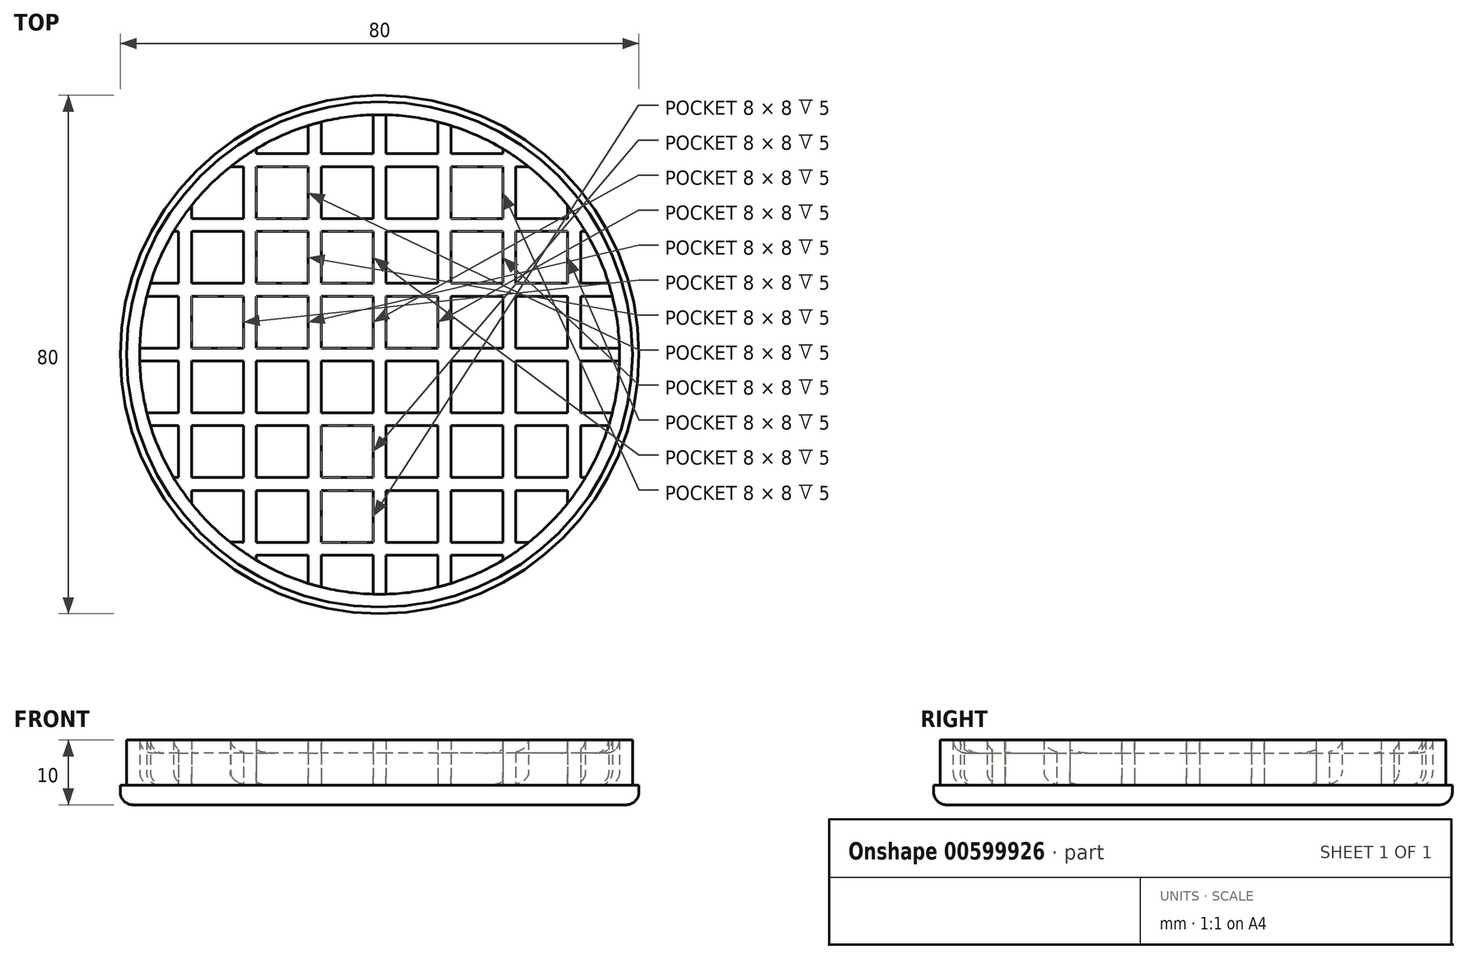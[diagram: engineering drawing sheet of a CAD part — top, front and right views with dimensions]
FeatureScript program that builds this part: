
annotation { "Feature Type Name" : "Feature", "Feature Type Description" : "" }
export const myFeature = defineFeature(function(context is Context, id is Id, definition is map)
    precondition{}
    {
        {
            var Q0;
            Q0=qCreatedBy(makeId("Front.planeOp"),FACE);
            var sketch = newSketch(context, id + "F0", { "sketchPlane" : qUnion([Q0])});
            skLineSegment(sketch, "E0", {"start": v(0, 0) * mm, "end": v(-38, 0) * mm});
            skLineSegment(sketch, "E1", {"start": v(-40, 2) * mm, "end": v(-40, 3) * mm});
            skLineSegment(sketch, "E2", {"start": v(-40, 3) * mm, "end": v(-39, 3) * mm});
            skLineSegment(sketch, "E3", {"start": v(-39, 3) * mm, "end": v(-39, 10) * mm});
            skLineSegment(sketch, "E4", {"start": v(-39, 10) * mm, "end": v(-37, 10) * mm});
            skLineSegment(sketch, "E5", {"start": v(0, 3) * mm, "end": v(0, 0) * mm});
            skPoint(sketch, "E6.visualSharp", {"position": v(-37, 3) * mm});
            skPoint(sketch, "E7.visualSharp", {"position": v(-40, 0) * mm});
            skArc(sketch, "E7.filletArc", {"start": v(-40, 2) * mm, "mid": v(-39.41, 0.59) * mm, "end": v(-38, 0) * mm});
            skLineSegment(sketch, "E8", {"start": v(-37, 10) * mm, "end": v(-37, 3) * mm});
            skLineSegment(sketch, "E9", {"start": v(-37, 3) * mm, "end": v(0, 3) * mm});
            skSolve(sketch);
        }
        {
            var Q0;
            Q0=makeQuery(id+"F0.imprint","IMPRINT",FACE,{"disambiguationData":[TD([[makeQuery(id+"F0.imprint","IMPRINT",EDGE,{"derivedFrom":sQuery(id+"F0.wireOp",EDGE,"E0")}),-1.0]])]});
            var Q1;
            Q1=sQuery(id+"F0.wireOp",EDGE,"E5");
            revolve(context, id + "F1", {"entities" : qUnion([Q0]), "axis" : qUnion([Q1]), "revolveType" : RevolveType.FULL});
        }
        {
            var Q0;
            Q0=makeQuery(id+"F1.opRevolve","SWEPT_FACE",FACE,{"disambiguationData":[OSD([sQuery(id+"F0.wireOp",EDGE,"E9")])]});
            var sketch = newSketch(context, id + "F2", { "sketchPlane" : qUnion([Q0])});
            skLineSegment(sketch, "E10", {"start": v(-1, 37.14) * mm, "end": v(-1, 21) * mm});
            skLineSegment(sketch, "E11", {"start": v(-9, 36.05) * mm, "end": v(-9, 31) * mm});
            skLineSegment(sketch, "E12", {"start": v(-19, 31.93) * mm, "end": v(-19, 31) * mm});
            skLineSegment(sketch, "E13", {"start": v(-11, 35.49) * mm, "end": v(-11, 31) * mm});
            skLineSegment(sketch, "E14", {"start": v(0, 63.51) * mm, "end": v(0, 19) * mm, "construction": true});
            skLineSegment(sketch, "E15.MirrorCS", {"start": v(29, 23.22) * mm, "end": v(29, 21) * mm});
            skLineSegment(sketch, "E16.MirrorCS", {"start": v(19, 31.93) * mm, "end": v(19, 31) * mm});
            skLineSegment(sketch, "E17.MirrorCS", {"start": v(11, 35.49) * mm, "end": v(11, 31) * mm});
            skLineSegment(sketch, "E18.MirrorCS", {"start": v(9, 36.05) * mm, "end": v(9, 31) * mm});
            skLineSegment(sketch, "E19.MirrorCS", {"start": v(1, 37.14) * mm, "end": v(1, 31) * mm});
            skArc(sketch, "E20", {"start": v(-9, 36.05) * mm, "mid": v(-10, 35.78) * mm, "end": v(-11, 35.49) * mm});
            skLineSegment(sketch, "E21", {"start": v(-46.87, 0) * mm, "end": v(0, 0) * mm, "construction": true});
            skLineSegment(sketch, "E22", {"start": v(-37.14, -1) * mm, "end": v(-31, -1) * mm});
            skLineSegment(sketch, "E23", {"start": v(-36.05, -9) * mm, "end": v(-31, -9) * mm});
            skLineSegment(sketch, "E24", {"start": v(-35.49, -11) * mm, "end": v(-31, -11) * mm});
            skLineSegment(sketch, "E25", {"start": v(-31.93, -19) * mm, "end": v(-31, -19) * mm});
            skLineSegment(sketch, "E26", {"start": v(-19, -31) * mm, "end": v(-11, -31) * mm});
            skLineSegment(sketch, "E27.MirrorCS", {"start": v(-37.14, 1) * mm, "end": v(-31, 1) * mm});
            skLineSegment(sketch, "E28.MirrorCS", {"start": v(-36.05, 9) * mm, "end": v(-31, 9) * mm});
            skLineSegment(sketch, "E29.MirrorCS", {"start": v(-31.93, 19) * mm, "end": v(-31, 19) * mm});
            skPoint(sketch, "E30.orphan", {"position": v(-11, 50.12) * mm});
            skPoint(sketch, "E31.orphan", {"position": v(-9, 38.7) * mm});
            skPoint(sketch, "E32.orphan", {"position": v(-1, 41.9) * mm});
            skPoint(sketch, "E33.orphan", {"position": v(1, 41.9) * mm});
            skPoint(sketch, "E34.orphan", {"position": v(9, 38.7) * mm});
            skPoint(sketch, "E35.orphan", {"position": v(11, 50.12) * mm});
            skPoint(sketch, "E36.orphan", {"position": v(-19, 39.94) * mm});
            skArc(sketch, "E37.trimOffspring", {"start": v(-19, 31.93) * mm, "mid": v(-21.16, 30.54) * mm, "end": v(-23.22, 29) * mm});
            skArc(sketch, "E38.trimOffspring", {"start": v(1, 37.14) * mm, "mid": v(0, 37.15) * mm, "end": v(-1, 37.14) * mm});
            skArc(sketch, "E39.trimOffspring", {"start": v(11, 35.49) * mm, "mid": v(10, 35.78) * mm, "end": v(9, 36.05) * mm});
            skPoint(sketch, "E40.orphan", {"position": v(21, 41.25) * mm});
            skPoint(sketch, "E41.orphan", {"position": v(19, 39.94) * mm});
            skPoint(sketch, "E42.orphan", {"position": v(22.5, 31) * mm});
            skPoint(sketch, "E43.orphan", {"position": v(28.03, 29) * mm});
            skLineSegment(sketch, "E44.trimOffspring", {"start": v(9, 29) * mm, "end": v(9, 21) * mm});
            skLineSegment(sketch, "E45.trimOffspring", {"start": v(11, 29) * mm, "end": v(19, 29) * mm});
            skLineSegment(sketch, "E46.trimOffspring", {"start": v(19, 29) * mm, "end": v(19, 21) * mm});
            skLineSegment(sketch, "E47.trimOffspring", {"start": v(21, 29) * mm, "end": v(23.22, 29) * mm});
            skLineSegment(sketch, "E48.trimOffspring", {"start": v(29, 19) * mm, "end": v(29, 11) * mm});
            skLineSegment(sketch, "E49.trimOffspring", {"start": v(31, 19) * mm, "end": v(31, 11) * mm});
            skLineSegment(sketch, "E50.trimOffspring", {"start": v(31, 19) * mm, "end": v(31.93, 19) * mm});
            skPoint(sketch, "E51.orphan", {"position": v(31, 33.97) * mm});
            skPoint(sketch, "E52.orphan", {"position": v(36.83, 21) * mm});
            skPoint(sketch, "E53.orphan", {"position": v(35.98, 19) * mm});
            skPoint(sketch, "E54.orphan", {"position": v(29, 34.3) * mm});
            skPoint(sketch, "E55.orphan", {"position": v(43.35, 11) * mm});
            skPoint(sketch, "E56.orphan", {"position": v(42.56, 9) * mm});
            skArc(sketch, "E57.trimOffspring", {"start": v(31.93, 19) * mm, "mid": v(30.54, 21.16) * mm, "end": v(29, 23.22) * mm});
            skArc(sketch, "E58.trimOffspring", {"start": v(23.22, 29) * mm, "mid": v(21.16, 30.54) * mm, "end": v(19, 31.93) * mm});
            skLineSegment(sketch, "E59", {"start": v(11, 31) * mm, "end": v(19, 31) * mm});
            skLineSegment(sketch, "E60.trimOffspring", {"start": v(21, 21) * mm, "end": v(29, 21) * mm});
            skLineSegment(sketch, "E61.trimOffspring", {"start": v(19, 19) * mm, "end": v(19, 11) * mm});
            skLineSegment(sketch, "E62.trimOffspring", {"start": v(21, 19) * mm, "end": v(21, 11) * mm});
            skLineSegment(sketch, "E63.trimOffspring", {"start": v(0, 11) * mm, "end": v(0, -20.11) * mm, "construction": true});
            skLineSegment(sketch, "E64.trimOffspring", {"start": v(11, 19) * mm, "end": v(11, 11) * mm});
            skLineSegment(sketch, "E65.trimOffspring", {"start": v(21, 19) * mm, "end": v(29, 19) * mm});
            skLineSegment(sketch, "E66.trimOffspring", {"start": v(9, 9) * mm, "end": v(9, 1) * mm});
            skLineSegment(sketch, "E67.trimOffspring", {"start": v(11, 19) * mm, "end": v(19, 19) * mm});
            skLineSegment(sketch, "E68", {"start": v(11, 29) * mm, "end": v(11, 21) * mm});
            skLineSegment(sketch, "E69.trimOffspring", {"start": v(11, 21) * mm, "end": v(19, 21) * mm});
            skLineSegment(sketch, "E70.trimOffspring", {"start": v(1, 21) * mm, "end": v(9, 21) * mm});
            skLineSegment(sketch, "E71.trimOffspring", {"start": v(1, 19) * mm, "end": v(1, 11) * mm});
            skLineSegment(sketch, "E72.trimOffspring", {"start": v(-1, 19) * mm, "end": v(-1, 11) * mm});
            skLineSegment(sketch, "E73.trimOffspring", {"start": v(1, 19) * mm, "end": v(9, 19) * mm});
            skLineSegment(sketch, "E74.trimOffspring", {"start": v(-9, 21) * mm, "end": v(-1, 21) * mm});
            skLineSegment(sketch, "E75.trimOffspring", {"start": v(-11, 19) * mm, "end": v(-11, 11) * mm});
            skLineSegment(sketch, "E76.trimOffspring", {"start": v(-9, 19) * mm, "end": v(-1, 19) * mm});
            skLineSegment(sketch, "E77.trimOffspring", {"start": v(-9, 19) * mm, "end": v(-9, 11) * mm});
            skLineSegment(sketch, "E78.trimOffspring", {"start": v(-9, 31) * mm, "end": v(-1, 31) * mm});
            skLineSegment(sketch, "E79.trimOffspring", {"start": v(-9, 29) * mm, "end": v(-9, 21) * mm});
            skLineSegment(sketch, "E80.trimOffspring", {"start": v(-9, 29) * mm, "end": v(-1, 29) * mm});
            skLineSegment(sketch, "E81.trimOffspring", {"start": v(-11, 29) * mm, "end": v(-11, 21) * mm});
            skLineSegment(sketch, "E82.trimOffspring", {"start": v(-9, 11) * mm, "end": v(-1, 11) * mm});
            skLineSegment(sketch, "E83.trimOffspring", {"start": v(-11, 9) * mm, "end": v(-11, 1) * mm});
            skLineSegment(sketch, "E84.trimOffspring", {"start": v(-9, 9) * mm, "end": v(-9, 1) * mm});
            skLineSegment(sketch, "E85", {"start": v(-19, 9) * mm, "end": v(-11, 9) * mm});
            skLineSegment(sketch, "E86.trimOffspring", {"start": v(-19, 11) * mm, "end": v(-11, 11) * mm});
            skLineSegment(sketch, "E87.trimOffspring", {"start": v(-21, 9) * mm, "end": v(-21, 1) * mm});
            skLineSegment(sketch, "E88.trimOffspring", {"start": v(-19, 9) * mm, "end": v(-19, 1) * mm});
            skLineSegment(sketch, "E89.trimOffspring", {"start": v(-31, 9) * mm, "end": v(-31, 1) * mm});
            skLineSegment(sketch, "E90.trimOffspring", {"start": v(-29, 11) * mm, "end": v(-21, 11) * mm});
            skLineSegment(sketch, "E91.trimOffspring", {"start": v(-29, 9) * mm, "end": v(-29, 1) * mm});
            skLineSegment(sketch, "E92.trimOffspring", {"start": v(-29, 9) * mm, "end": v(-21, 9) * mm});
            skLineSegment(sketch, "E93.trimOffspring", {"start": v(-31, 19) * mm, "end": v(-31, 11) * mm});
            skLineSegment(sketch, "E94.trimOffspring", {"start": v(-29, 21) * mm, "end": v(-21, 21) * mm});
            skPoint(sketch, "E95.MirrorCS.start.orphan", {"position": v(-37.13, 21) * mm});
            skLineSegment(sketch, "E96.trimOffspring", {"start": v(-29, 19) * mm, "end": v(-21, 19) * mm});
            skLineSegment(sketch, "E97.trimOffspring", {"start": v(-29, 19) * mm, "end": v(-29, 11) * mm});
            skPoint(sketch, "E98.orphan", {"position": v(-37.52, 19) * mm});
            skArc(sketch, "E99.trimOffspring", {"start": v(-35.49, 11) * mm, "mid": v(-35.78, 10) * mm, "end": v(-36.05, 9) * mm});
            skArc(sketch, "E100.trimOffspring", {"start": v(-29, 23.22) * mm, "mid": v(-30.54, 21.16) * mm, "end": v(-31.93, 19) * mm});
            skLineSegment(sketch, "E101.trimOffspring", {"start": v(-19, 31) * mm, "end": v(-11, 31) * mm});
            skPoint(sketch, "E102.MirrorCS.start.orphan", {"position": v(-27.7, 31) * mm});
            skPoint(sketch, "E103.start.orphan", {"position": v(-21, 41.25) * mm});
            skLineSegment(sketch, "E104.trimOffspring", {"start": v(-23.22, 29) * mm, "end": v(-21, 29) * mm});
            skLineSegment(sketch, "E105.trimOffspring", {"start": v(-19, 29) * mm, "end": v(-11, 29) * mm});
            skLineSegment(sketch, "E106.trimOffspring", {"start": v(-19, 29) * mm, "end": v(-19, 21) * mm});
            skArc(sketch, "E107.trimOffspring", {"start": v(36.05, 9) * mm, "mid": v(35.78, 10) * mm, "end": v(35.49, 11) * mm});
            skArc(sketch, "E108.trimOffspring", {"start": v(37.14, -1) * mm, "mid": v(37.15, 0) * mm, "end": v(37.14, 1) * mm});
            skLineSegment(sketch, "E109.trimOffspring", {"start": v(31, 1) * mm, "end": v(37.14, 1) * mm});
            skLineSegment(sketch, "E110.trimOffspring", {"start": v(29, -1) * mm, "end": v(29, -9) * mm});
            skLineSegment(sketch, "E111.trimOffspring", {"start": v(31, -1) * mm, "end": v(31, -9) * mm});
            skLineSegment(sketch, "E112.trimOffspring", {"start": v(37.15, 0) * mm, "end": v(44.83, 0) * mm, "construction": true});
            skLineSegment(sketch, "E113.trimOffspring", {"start": v(31, 9) * mm, "end": v(31, 1) * mm});
            skLineSegment(sketch, "E114.trimOffspring", {"start": v(31, 11) * mm, "end": v(35.49, 11) * mm});
            skLineSegment(sketch, "E115.trimOffspring", {"start": v(31, 9) * mm, "end": v(36.05, 9) * mm});
            skLineSegment(sketch, "E116.trimOffspring", {"start": v(29, 9) * mm, "end": v(29, 1) * mm});
            skLineSegment(sketch, "E117.trimOffspring", {"start": v(21, 9) * mm, "end": v(21, 1) * mm});
            skLineSegment(sketch, "E118.trimOffspring", {"start": v(21, 11) * mm, "end": v(29, 11) * mm});
            skLineSegment(sketch, "E119.trimOffspring", {"start": v(19, 9) * mm, "end": v(19, 1) * mm});
            skLineSegment(sketch, "E120.trimOffspring", {"start": v(21, 9) * mm, "end": v(29, 9) * mm});
            skLineSegment(sketch, "E121", {"start": v(9, 11) * mm, "end": v(9, 19) * mm});
            skLineSegment(sketch, "E122.trimOffspring", {"start": v(11, 9) * mm, "end": v(11, 1) * mm});
            skLineSegment(sketch, "E123.trimOffspring", {"start": v(11, 11) * mm, "end": v(19, 11) * mm});
            skLineSegment(sketch, "E124.trimOffspring", {"start": v(11, 9) * mm, "end": v(19, 9) * mm});
            skLineSegment(sketch, "E125.trimOffspring", {"start": v(1, 11) * mm, "end": v(9, 11) * mm});
            skLineSegment(sketch, "E126.trimOffspring", {"start": v(1, 9) * mm, "end": v(9, 9) * mm});
            skLineSegment(sketch, "E127.trimOffspring", {"start": v(1, 9) * mm, "end": v(1, 1) * mm});
            skLineSegment(sketch, "E128.trimOffspring", {"start": v(-1, 9) * mm, "end": v(-1, 1) * mm});
            skLineSegment(sketch, "E129", {"start": v(-19, 21) * mm, "end": v(-11, 21) * mm});
            skLineSegment(sketch, "E130.trimOffspring", {"start": v(-21, 19) * mm, "end": v(-21, 11) * mm});
            skLineSegment(sketch, "E131.trimOffspring", {"start": v(-19, 19) * mm, "end": v(-11, 19) * mm});
            skLineSegment(sketch, "E132.trimOffspring", {"start": v(-19, 19) * mm, "end": v(-19, 11) * mm});
            skLineSegment(sketch, "E133", {"start": v(-21, 29) * mm, "end": v(-21, 21) * mm});
            skLineSegment(sketch, "E134.trimOffspring", {"start": v(-31, -1) * mm, "end": v(-31, -9) * mm});
            skPoint(sketch, "E135.orphan", {"position": v(-42.4, 11) * mm});
            skLineSegment(sketch, "E136.trimOffspring", {"start": v(-29, 1) * mm, "end": v(-21, 1) * mm});
            skLineSegment(sketch, "E137.trimOffspring", {"start": v(-29, -1) * mm, "end": v(-29, -9) * mm});
            skPoint(sketch, "E138.orphan", {"position": v(-41.5, 1) * mm});
            skPoint(sketch, "E139.orphan", {"position": v(-41.5, -1) * mm});
            skArc(sketch, "E140.trimOffspring", {"start": v(-37.14, 1) * mm, "mid": v(-37.15, 0) * mm, "end": v(-37.14, -1) * mm});
            skArc(sketch, "E141.trimOffspring", {"start": v(-36.05, -9) * mm, "mid": v(-35.78, -10) * mm, "end": v(-35.49, -11) * mm});
            skPoint(sketch, "E142.orphan", {"position": v(-38.6, 9) * mm});
            skLineSegment(sketch, "E143.trimOffspring", {"start": v(-29, 23.22) * mm, "end": v(-29, 21) * mm});
            skPoint(sketch, "E144.MirrorCS.start.orphan", {"position": v(-33.6, 29) * mm});
            skPoint(sketch, "E145.start.orphan", {"position": v(-31, 33.97) * mm});
            skPoint(sketch, "E146.start.orphan", {"position": v(-29, 34.3) * mm});
            skPoint(sketch, "E147.orphan", {"position": v(-38.6, -9) * mm});
            skPoint(sketch, "E148.orphan", {"position": v(-42.4, -11) * mm});
            skArc(sketch, "E149.trimOffspring", {"start": v(-31.93, -19) * mm, "mid": v(-30.54, -21.16) * mm, "end": v(-29, -23.22) * mm});
            skLineSegment(sketch, "E150.trimOffspring", {"start": v(-29, -9) * mm, "end": v(-21, -9) * mm});
            skLineSegment(sketch, "E151.trimOffspring", {"start": v(-31, -11) * mm, "end": v(-31, -19) * mm});
            skLineSegment(sketch, "E152.trimOffspring", {"start": v(-29, -11) * mm, "end": v(-29, -19) * mm});
            skLineSegment(sketch, "E153.trimOffspring", {"start": v(-29, -11) * mm, "end": v(-21, -11) * mm});
            skPoint(sketch, "E154.orphan", {"position": v(-37.52, -19) * mm});
            skPoint(sketch, "E155.orphan", {"position": v(-37.13, -21) * mm});
            skArc(sketch, "E156.trimOffspring", {"start": v(-23.22, -29) * mm, "mid": v(-21.16, -30.54) * mm, "end": v(-19, -31.93) * mm});
            skLineSegment(sketch, "E157.trimOffspring", {"start": v(-29, -21) * mm, "end": v(-29, -23.22) * mm});
            skLineSegment(sketch, "E158.trimOffspring", {"start": v(-29, -19) * mm, "end": v(-21, -19) * mm});
            skLineSegment(sketch, "E159.trimOffspring", {"start": v(-29, -21) * mm, "end": v(-21, -21) * mm});
            skLineSegment(sketch, "E160.trimOffspring", {"start": v(-19, -29) * mm, "end": v(-11, -29) * mm});
            skPoint(sketch, "E161.orphan", {"position": v(-33.6, -29) * mm});
            skPoint(sketch, "E162.trimOffspring.end.orphan", {"position": v(-31, -35.22) * mm});
            skPoint(sketch, "E163.trimOffspring.end.orphan", {"position": v(-29, -33.7) * mm});
            skPoint(sketch, "E164.orphan", {"position": v(-27.7, -31) * mm});
            skPoint(sketch, "E165.orphan", {"position": v(-21, -41.31) * mm});
            skPoint(sketch, "E166.orphan", {"position": v(-19, -40.4) * mm});
            skArc(sketch, "E167.trimOffspring", {"start": v(-11, -35.49) * mm, "mid": v(-10, -35.78) * mm, "end": v(-9, -36.05) * mm});
            skLineSegment(sketch, "E168.trimOffspring", {"start": v(-19, -31) * mm, "end": v(-19, -31.93) * mm});
            skLineSegment(sketch, "E169", {"start": v(-23.3, -28.94) * mm, "end": v(-21, -28.97) * mm});
            skLineSegment(sketch, "E170", {"start": v(-21, -21) * mm, "end": v(-21, -28.97) * mm});
            skLineSegment(sketch, "E171.trimOffspring", {"start": v(-19, -21) * mm, "end": v(-11, -21) * mm});
            skLineSegment(sketch, "E172.trimOffspring", {"start": v(-19, -21) * mm, "end": v(-19, -29) * mm});
            skLineSegment(sketch, "E173.trimOffspring", {"start": v(-19, -19) * mm, "end": v(-11, -19) * mm});
            skLineSegment(sketch, "E174.trimOffspring", {"start": v(-21, -1) * mm, "end": v(-21, -9) * mm});
            skLineSegment(sketch, "E175.trimOffspring", {"start": v(-19, 1) * mm, "end": v(-11, 1) * mm});
            skLineSegment(sketch, "E176.trimOffspring", {"start": v(-19, -1) * mm, "end": v(-19, -9) * mm});
            skLineSegment(sketch, "E177.trimOffspring", {"start": v(-19, -1) * mm, "end": v(-11, -1) * mm});
            skLineSegment(sketch, "E178.trimOffspring", {"start": v(-11, -1) * mm, "end": v(-11, -9) * mm});
            skLineSegment(sketch, "E179.trimOffspring", {"start": v(-9, -1) * mm, "end": v(-9, -9) * mm});
            skLineSegment(sketch, "E180.trimOffspring", {"start": v(-9, -1) * mm, "end": v(-1, -1) * mm});
            skLineSegment(sketch, "E181.trimOffspring", {"start": v(-1, -11) * mm, "end": v(-1, -19) * mm});
            skLineSegment(sketch, "E182.trimOffspring", {"start": v(1, 1) * mm, "end": v(9, 1) * mm});
            skLineSegment(sketch, "E183.trimOffspring", {"start": v(1, -1) * mm, "end": v(1, -9) * mm});
            skLineSegment(sketch, "E184.trimOffspring", {"start": v(1, -1) * mm, "end": v(9, -1) * mm});
            skLineSegment(sketch, "E185", {"start": v(-9, 9) * mm, "end": v(-1, 9) * mm});
            skLineSegment(sketch, "E186", {"start": v(-9, 1) * mm, "end": v(-1, 1) * mm});
            skLineSegment(sketch, "E187", {"start": v(-1, -1) * mm, "end": v(-1, -9) * mm});
            skLineSegment(sketch, "E188.trimOffspring", {"start": v(1, -9) * mm, "end": v(9, -9) * mm});
            skLineSegment(sketch, "E189.trimOffspring", {"start": v(1, -11) * mm, "end": v(1, -19) * mm});
            skLineSegment(sketch, "E190.trimOffspring", {"start": v(1, -11) * mm, "end": v(9, -11) * mm});
            skLineSegment(sketch, "E191.trimOffspring", {"start": v(-11, -11) * mm, "end": v(-11, -19) * mm});
            skLineSegment(sketch, "E192.trimOffspring", {"start": v(-9, -9) * mm, "end": v(-1, -9) * mm});
            skLineSegment(sketch, "E193.trimOffspring", {"start": v(-9, -11) * mm, "end": v(-9, -19) * mm});
            skLineSegment(sketch, "E194.trimOffspring", {"start": v(-9, -11) * mm, "end": v(-1, -11) * mm});
            skLineSegment(sketch, "E195.trimOffspring", {"start": v(-1, -21) * mm, "end": v(-1, -29) * mm});
            skLineSegment(sketch, "E196.trimOffspring", {"start": v(1, -19) * mm, "end": v(9, -19) * mm});
            skLineSegment(sketch, "E197.trimOffspring", {"start": v(1, -21) * mm, "end": v(1, -29) * mm});
            skLineSegment(sketch, "E198.trimOffspring", {"start": v(1, -21) * mm, "end": v(9, -21) * mm});
            skLineSegment(sketch, "E199.trimOffspring", {"start": v(-9, -19) * mm, "end": v(-1, -19) * mm});
            skLineSegment(sketch, "E200.trimOffspring", {"start": v(-9, -21) * mm, "end": v(-9, -29) * mm});
            skLineSegment(sketch, "E201.trimOffspring", {"start": v(-9, -21) * mm, "end": v(-1, -21) * mm});
            skLineSegment(sketch, "E202.trimOffspring", {"start": v(-11, -21) * mm, "end": v(-11, -29) * mm});
            skLineSegment(sketch, "E203.trimOffspring", {"start": v(-9, -29) * mm, "end": v(-1, -29) * mm});
            skLineSegment(sketch, "E204.trimOffspring", {"start": v(-9, -31) * mm, "end": v(-9, -36.05) * mm});
            skLineSegment(sketch, "E205.trimOffspring", {"start": v(-9, -31) * mm, "end": v(-1, -31) * mm});
            skLineSegment(sketch, "E206.trimOffspring", {"start": v(-11, -31) * mm, "end": v(-11, -35.49) * mm});
            skPoint(sketch, "E207.orphan", {"position": v(-11, -37.88) * mm});
            skPoint(sketch, "E208.orphan", {"position": v(-9, -46.3) * mm});
            skArc(sketch, "E209.trimOffspring", {"start": v(-1, -37.14) * mm, "mid": v(0, -37.15) * mm, "end": v(1, -37.14) * mm});
            skPoint(sketch, "E210.orphan", {"position": v(-1, -43.1) * mm});
            skPoint(sketch, "E211.orphan", {"position": v(1, -43.1) * mm});
            skArc(sketch, "E212.trimOffspring", {"start": v(9, -36.05) * mm, "mid": v(10, -35.78) * mm, "end": v(11, -35.49) * mm});
            skLineSegment(sketch, "E213.trimOffspring", {"start": v(11, -31) * mm, "end": v(19, -31) * mm});
            skLineSegment(sketch, "E214.trimOffspring", {"start": v(-1, -31) * mm, "end": v(-1, -37.14) * mm});
            skLineSegment(sketch, "E215.trimOffspring", {"start": v(1, -29) * mm, "end": v(9, -29) * mm});
            skLineSegment(sketch, "E216.trimOffspring", {"start": v(1, -31) * mm, "end": v(1, -37.14) * mm});
            skLineSegment(sketch, "E217.trimOffspring", {"start": v(-21, -11) * mm, "end": v(-21, -19) * mm});
            skLineSegment(sketch, "E218.trimOffspring", {"start": v(-19, -9) * mm, "end": v(-11, -9) * mm});
            skLineSegment(sketch, "E219.trimOffspring", {"start": v(-19, -11) * mm, "end": v(-19, -19) * mm});
            skLineSegment(sketch, "E220.trimOffspring", {"start": v(-19, -11) * mm, "end": v(-11, -11) * mm});
            skLineSegment(sketch, "E221.trimOffspring", {"start": v(1, 31) * mm, "end": v(9, 31) * mm});
            skLineSegment(sketch, "E222.trimOffspring", {"start": v(1, 29) * mm, "end": v(1, 21) * mm});
            skLineSegment(sketch, "E223.trimOffspring", {"start": v(1, 29) * mm, "end": v(9, 29) * mm});
            skLineSegment(sketch, "E224.trimOffspring", {"start": v(11, 1) * mm, "end": v(19, 1) * mm});
            skLineSegment(sketch, "E225.trimOffspring", {"start": v(9, -1) * mm, "end": v(9, -9) * mm});
            skLineSegment(sketch, "E226.trimOffspring", {"start": v(11, -1) * mm, "end": v(11, -9) * mm});
            skLineSegment(sketch, "E227.trimOffspring", {"start": v(11, -1) * mm, "end": v(19, -1) * mm});
            skLineSegment(sketch, "E228.trimOffspring", {"start": v(19, -1) * mm, "end": v(19, -9) * mm});
            skLineSegment(sketch, "E229.trimOffspring", {"start": v(21, -1) * mm, "end": v(29, -1) * mm});
            skLineSegment(sketch, "E230.trimOffspring", {"start": v(21, -1) * mm, "end": v(21, -9) * mm});
            skLineSegment(sketch, "E231.trimOffspring", {"start": v(21, 1) * mm, "end": v(29, 1) * mm});
            skLineSegment(sketch, "E232", {"start": v(21, 29) * mm, "end": v(21, 21) * mm});
            skPoint(sketch, "E233.orphan", {"position": v(44.83, 1) * mm});
            skPoint(sketch, "E234.orphan", {"position": v(44.83, -1) * mm});
            skLineSegment(sketch, "E235", {"start": v(31, -1) * mm, "end": v(37.14, -1) * mm});
            skArc(sketch, "E236.trimOffspring", {"start": v(35.49, -11) * mm, "mid": v(35.78, -10) * mm, "end": v(36.05, -9) * mm});
            skPoint(sketch, "E237.orphan", {"position": v(43.35, -11) * mm});
            skPoint(sketch, "E238.orphan", {"position": v(42.56, -9) * mm});
            skLineSegment(sketch, "E239.trimOffspring", {"start": v(31, -11) * mm, "end": v(35.49, -11) * mm});
            skLineSegment(sketch, "E240.trimOffspring", {"start": v(29, -11) * mm, "end": v(29, -19) * mm});
            skLineSegment(sketch, "E241.trimOffspring", {"start": v(31, -9) * mm, "end": v(36.05, -9) * mm});
            skLineSegment(sketch, "E242.trimOffspring", {"start": v(31, -11) * mm, "end": v(31, -19) * mm});
            skPoint(sketch, "E243.orphan", {"position": v(36.83, -21) * mm});
            skPoint(sketch, "E244.orphan", {"position": v(29, -33.7) * mm});
            skPoint(sketch, "E245.orphan", {"position": v(31, -35.22) * mm});
            skPoint(sketch, "E246.orphan", {"position": v(35.98, -19) * mm});
            skArc(sketch, "E247.trimOffspring", {"start": v(29, -23.22) * mm, "mid": v(30.54, -21.16) * mm, "end": v(31.93, -19) * mm});
            skLineSegment(sketch, "E248.trimOffspring", {"start": v(31, -19) * mm, "end": v(31.93, -19) * mm});
            skLineSegment(sketch, "E249.trimOffspring", {"start": v(29, -21) * mm, "end": v(29, -23.22) * mm});
            skLineSegment(sketch, "E250.trimOffspring", {"start": v(21, -9) * mm, "end": v(29, -9) * mm});
            skLineSegment(sketch, "E251.trimOffspring", {"start": v(19, -11) * mm, "end": v(19, -19) * mm});
            skLineSegment(sketch, "E252.trimOffspring", {"start": v(21, -11) * mm, "end": v(29, -11) * mm});
            skLineSegment(sketch, "E253.trimOffspring", {"start": v(21, -11) * mm, "end": v(21, -19) * mm});
            skLineSegment(sketch, "E254.trimOffspring", {"start": v(21, -19) * mm, "end": v(29, -19) * mm});
            skLineSegment(sketch, "E255.trimOffspring", {"start": v(21, -21) * mm, "end": v(29, -21) * mm});
            skLineSegment(sketch, "E256.trimOffspring", {"start": v(19, -21) * mm, "end": v(19, -29) * mm});
            skLineSegment(sketch, "E257.trimOffspring", {"start": v(21, -21) * mm, "end": v(21, -29) * mm});
            skPoint(sketch, "E258.orphan", {"position": v(28.03, -29) * mm});
            skPoint(sketch, "E259.orphan", {"position": v(21, -41.31) * mm});
            skPoint(sketch, "E260.orphan", {"position": v(22.5, -31) * mm});
            skPoint(sketch, "E261.orphan", {"position": v(19, -40.4) * mm});
            skLineSegment(sketch, "E262.trimOffspring", {"start": v(19, -31) * mm, "end": v(19, -31.93) * mm});
            skLineSegment(sketch, "E263.trimOffspring", {"start": v(21, -29) * mm, "end": v(23.22, -29) * mm});
            skPoint(sketch, "E264.orphan", {"position": v(11, -37.88) * mm});
            skPoint(sketch, "E265.orphan", {"position": v(9, -46.3) * mm});
            skArc(sketch, "E266.trimOffspring", {"start": v(19, -31.93) * mm, "mid": v(21.16, -30.54) * mm, "end": v(23.22, -29) * mm});
            skLineSegment(sketch, "E267", {"start": v(1, -31) * mm, "end": v(9, -31) * mm});
            skLineSegment(sketch, "E268.trimOffspring", {"start": v(9, -31) * mm, "end": v(9, -36.05) * mm});
            skLineSegment(sketch, "E269.trimOffspring", {"start": v(11, -29) * mm, "end": v(19, -29) * mm});
            skLineSegment(sketch, "E270.trimOffspring", {"start": v(11, -31) * mm, "end": v(11, -35.49) * mm});
            skLineSegment(sketch, "E271.trimOffspring", {"start": v(11, -19) * mm, "end": v(19, -19) * mm});
            skLineSegment(sketch, "E272.trimOffspring", {"start": v(11, -21) * mm, "end": v(11, -29) * mm});
            skLineSegment(sketch, "E273.trimOffspring", {"start": v(11, -21) * mm, "end": v(19, -21) * mm});
            skLineSegment(sketch, "E274.trimOffspring", {"start": v(9, -21) * mm, "end": v(9, -29) * mm});
            skLineSegment(sketch, "E275", {"start": v(-35.49, 11) * mm, "end": v(-31, 11) * mm});
            skLineSegment(sketch, "E276.trimOffspring", {"start": v(11, -9) * mm, "end": v(19, -9) * mm});
            skLineSegment(sketch, "E277.trimOffspring", {"start": v(9, -11) * mm, "end": v(9, -19) * mm});
            skLineSegment(sketch, "E278.trimOffspring", {"start": v(11, -11) * mm, "end": v(19, -11) * mm});
            skLineSegment(sketch, "E279.trimOffspring", {"start": v(11, -11) * mm, "end": v(11, -19) * mm});
            skLineSegment(sketch, "E280", {"start": v(-29, -1) * mm, "end": v(-21, -1) * mm});
            skSolve(sketch);
        }
        {
            var Q0;
            {var subQ28=sQuery(id+"F2.wireOp",EDGE,"E26");Q0=makeQuery(id+"F2.imprint","IMPRINT",FACE,{"disambiguationData":[TD([[makeQuery(id+"F2.imprint","IMPRINT",EDGE,{"derivedFrom":subQ28}),1.0]])]});}
            var Q1;
            Q1=makeQuery(id+"F1.opRevolve","SWEPT_FACE",FACE,{"disambiguationData":[OSD([sQuery(id+"F0.wireOp",EDGE,"E4")])]});
            extrude(context, id + "F3", {"entities" : qUnion([Q0]), "operationType" : NewBodyOperationType.ADD, "endBound" : BoundingType.UP_TO_SURFACE, "depth" : 25 * mm, "endBoundEntityFace" : qUnion([Q1]), "offsetDistance" : 25 * mm});
        }
        {
            var Q0;
            {var subQ0=sQuery(id+"F0.wireOp",EDGE,"E8");var subQ1=sQuery(id+"F0.wireOp",EDGE,"E9");Q0=makeQuery(id+"F3.boolean.opBoolean","SPLIT",EDGE,{"disambiguationData":[TD([makeQuery(id+"F3.opExtrude","SWEPT_FACE",FACE,{"disambiguationData":[OSD([sQuery(id+"F2.wireOp",EDGE,"E104.trimOffspring")])]})])],"derivedFrom":makeQuery(id+"F1.opRevolve","SWEPT_EDGE",EDGE,{"disambiguationData":[OSD([subQ0,subQ1])]})});}
            var Q1;
            {var subQ0=sQuery(id+"F0.wireOp",EDGE,"E8");var subQ1=sQuery(id+"F0.wireOp",EDGE,"E9");Q1=makeQuery(id+"F3.boolean.opBoolean","SPLIT",EDGE,{"disambiguationData":[TD([makeQuery(id+"F3.opExtrude","SWEPT_FACE",FACE,{"disambiguationData":[OSD([sQuery(id+"F2.wireOp",EDGE,"E12")])]})])],"derivedFrom":makeQuery(id+"F1.opRevolve","SWEPT_EDGE",EDGE,{"disambiguationData":[OSD([subQ0,subQ1])]})});}
            var Q2;
            {var subQ0=sQuery(id+"F0.wireOp",EDGE,"E8");var subQ1=sQuery(id+"F0.wireOp",EDGE,"E9");Q2=makeQuery(id+"F3.boolean.opBoolean","SPLIT",EDGE,{"disambiguationData":[TD([makeQuery(id+"F3.opExtrude","SWEPT_FACE",FACE,{"disambiguationData":[OSD([sQuery(id+"F2.wireOp",EDGE,"E29.MirrorCS")])]})])],"derivedFrom":makeQuery(id+"F1.opRevolve","SWEPT_EDGE",EDGE,{"disambiguationData":[OSD([subQ0,subQ1])]})});}
            var Q3;
            {var subQ0=sQuery(id+"F0.wireOp",EDGE,"E8");var subQ1=sQuery(id+"F0.wireOp",EDGE,"E9");Q3=makeQuery(id+"F3.boolean.opBoolean","SPLIT",EDGE,{"disambiguationData":[TD([makeQuery(id+"F3.opExtrude","SWEPT_FACE",FACE,{"disambiguationData":[OSD([sQuery(id+"F2.wireOp",EDGE,"E27.MirrorCS")])]})])],"derivedFrom":makeQuery(id+"F1.opRevolve","SWEPT_EDGE",EDGE,{"disambiguationData":[OSD([subQ0,subQ1])]})});}
            var Q4;
            {var subQ0=sQuery(id+"F0.wireOp",EDGE,"E8");var subQ1=sQuery(id+"F0.wireOp",EDGE,"E9");Q4=makeQuery(id+"F3.boolean.opBoolean","SPLIT",EDGE,{"disambiguationData":[TD([makeQuery(id+"F3.opExtrude","SWEPT_FACE",FACE,{"disambiguationData":[OSD([sQuery(id+"F2.wireOp",EDGE,"E22")])]})])],"derivedFrom":makeQuery(id+"F1.opRevolve","SWEPT_EDGE",EDGE,{"disambiguationData":[OSD([subQ0,subQ1])]})});}
            var Q5;
            {var subQ0=sQuery(id+"F0.wireOp",EDGE,"E8");var subQ1=sQuery(id+"F0.wireOp",EDGE,"E9");Q5=makeQuery(id+"F3.boolean.opBoolean","SPLIT",EDGE,{"disambiguationData":[TD([makeQuery(id+"F3.opExtrude","SWEPT_FACE",FACE,{"disambiguationData":[OSD([sQuery(id+"F2.wireOp",EDGE,"E24")])]})])],"derivedFrom":makeQuery(id+"F1.opRevolve","SWEPT_EDGE",EDGE,{"disambiguationData":[OSD([subQ0,subQ1])]})});}
            var Q6;
            {var subQ0=sQuery(id+"F0.wireOp",EDGE,"E8");var subQ1=sQuery(id+"F0.wireOp",EDGE,"E9");Q6=makeQuery(id+"F3.boolean.opBoolean","SPLIT",EDGE,{"disambiguationData":[TD([makeQuery(id+"F3.opExtrude","SWEPT_FACE",FACE,{"disambiguationData":[OSD([sQuery(id+"F2.wireOp",EDGE,"E157.trimOffspring")])]})])],"derivedFrom":makeQuery(id+"F1.opRevolve","SWEPT_EDGE",EDGE,{"disambiguationData":[OSD([subQ0,subQ1])]})});}
            var Q7;
            {var subQ0=sQuery(id+"F0.wireOp",EDGE,"E8");var subQ1=sQuery(id+"F0.wireOp",EDGE,"E9");Q7=makeQuery(id+"F3.boolean.opBoolean","SPLIT",EDGE,{"disambiguationData":[TD([makeQuery(id+"F3.opExtrude","SWEPT_FACE",FACE,{"disambiguationData":[OSD([sQuery(id+"F2.wireOp",EDGE,"E168.trimOffspring")])]})])],"derivedFrom":makeQuery(id+"F1.opRevolve","SWEPT_EDGE",EDGE,{"disambiguationData":[OSD([subQ0,subQ1])]})});}
            var Q8;
            {var subQ0=sQuery(id+"F0.wireOp",EDGE,"E8");var subQ1=sQuery(id+"F0.wireOp",EDGE,"E9");Q8=makeQuery(id+"F3.boolean.opBoolean","SPLIT",EDGE,{"disambiguationData":[TD([makeQuery(id+"F3.opExtrude","SWEPT_FACE",FACE,{"disambiguationData":[OSD([sQuery(id+"F2.wireOp",EDGE,"E204.trimOffspring")])]})])],"derivedFrom":makeQuery(id+"F1.opRevolve","SWEPT_EDGE",EDGE,{"disambiguationData":[OSD([subQ0,subQ1])]})});}
            var Q9;
            {var subQ0=sQuery(id+"F0.wireOp",EDGE,"E8");var subQ1=sQuery(id+"F0.wireOp",EDGE,"E9");Q9=makeQuery(id+"F3.boolean.opBoolean","SPLIT",EDGE,{"disambiguationData":[TD([makeQuery(id+"F3.opExtrude","SWEPT_FACE",FACE,{"disambiguationData":[OSD([sQuery(id+"F2.wireOp",EDGE,"E216.trimOffspring")])]})])],"derivedFrom":makeQuery(id+"F1.opRevolve","SWEPT_EDGE",EDGE,{"disambiguationData":[OSD([subQ0,subQ1])]})});}
            var Q10;
            {var subQ0=sQuery(id+"F0.wireOp",EDGE,"E8");var subQ1=sQuery(id+"F0.wireOp",EDGE,"E9");Q10=makeQuery(id+"F3.boolean.opBoolean","SPLIT",EDGE,{"disambiguationData":[TD([makeQuery(id+"F3.opExtrude","SWEPT_FACE",FACE,{"disambiguationData":[OSD([sQuery(id+"F2.wireOp",EDGE,"E262.trimOffspring")])]})])],"derivedFrom":makeQuery(id+"F1.opRevolve","SWEPT_EDGE",EDGE,{"disambiguationData":[OSD([subQ0,subQ1])]})});}
            var Q11;
            {var subQ0=sQuery(id+"F0.wireOp",EDGE,"E8");var subQ1=sQuery(id+"F0.wireOp",EDGE,"E9");Q11=makeQuery(id+"F3.boolean.opBoolean","SPLIT",EDGE,{"disambiguationData":[TD([makeQuery(id+"F3.opExtrude","SWEPT_FACE",FACE,{"disambiguationData":[OSD([sQuery(id+"F2.wireOp",EDGE,"E249.trimOffspring")])]})])],"derivedFrom":makeQuery(id+"F1.opRevolve","SWEPT_EDGE",EDGE,{"disambiguationData":[OSD([subQ0,subQ1])]})});}
            var Q12;
            {var subQ0=sQuery(id+"F0.wireOp",EDGE,"E8");var subQ1=sQuery(id+"F0.wireOp",EDGE,"E9");Q12=makeQuery(id+"F3.boolean.opBoolean","SPLIT",EDGE,{"disambiguationData":[TD([makeQuery(id+"F3.opExtrude","SWEPT_FACE",FACE,{"disambiguationData":[OSD([sQuery(id+"F2.wireOp",EDGE,"E239.trimOffspring")])]})])],"derivedFrom":makeQuery(id+"F1.opRevolve","SWEPT_EDGE",EDGE,{"disambiguationData":[OSD([subQ0,subQ1])]})});}
            var Q13;
            {var subQ0=sQuery(id+"F0.wireOp",EDGE,"E8");var subQ1=sQuery(id+"F0.wireOp",EDGE,"E9");Q13=makeQuery(id+"F3.boolean.opBoolean","SPLIT",EDGE,{"disambiguationData":[TD([makeQuery(id+"F3.opExtrude","SWEPT_FACE",FACE,{"disambiguationData":[OSD([sQuery(id+"F2.wireOp",EDGE,"E235")])]})])],"derivedFrom":makeQuery(id+"F1.opRevolve","SWEPT_EDGE",EDGE,{"disambiguationData":[OSD([subQ0,subQ1])]})});}
            var Q14;
            {var subQ0=sQuery(id+"F0.wireOp",EDGE,"E8");var subQ1=sQuery(id+"F0.wireOp",EDGE,"E9");Q14=makeQuery(id+"F3.boolean.opBoolean","SPLIT",EDGE,{"disambiguationData":[TD([makeQuery(id+"F3.opExtrude","SWEPT_FACE",FACE,{"disambiguationData":[OSD([sQuery(id+"F2.wireOp",EDGE,"E109.trimOffspring")])]})])],"derivedFrom":makeQuery(id+"F1.opRevolve","SWEPT_EDGE",EDGE,{"disambiguationData":[OSD([subQ0,subQ1])]})});}
            var Q15;
            {var subQ0=sQuery(id+"F0.wireOp",EDGE,"E8");var subQ1=sQuery(id+"F0.wireOp",EDGE,"E9");Q15=makeQuery(id+"F3.boolean.opBoolean","SPLIT",EDGE,{"disambiguationData":[TD([makeQuery(id+"F3.opExtrude","SWEPT_FACE",FACE,{"disambiguationData":[OSD([sQuery(id+"F2.wireOp",EDGE,"E50.trimOffspring")])]})])],"derivedFrom":makeQuery(id+"F1.opRevolve","SWEPT_EDGE",EDGE,{"disambiguationData":[OSD([subQ0,subQ1])]})});}
            var Q16;
            {var subQ0=sQuery(id+"F0.wireOp",EDGE,"E8");var subQ1=sQuery(id+"F0.wireOp",EDGE,"E9");Q16=makeQuery(id+"F3.boolean.opBoolean","SPLIT",EDGE,{"disambiguationData":[TD([makeQuery(id+"F3.opExtrude","SWEPT_FACE",FACE,{"disambiguationData":[OSD([sQuery(id+"F2.wireOp",EDGE,"E15.MirrorCS")])]})])],"derivedFrom":makeQuery(id+"F1.opRevolve","SWEPT_EDGE",EDGE,{"disambiguationData":[OSD([subQ0,subQ1])]})});}
            var Q17;
            {var subQ0=sQuery(id+"F0.wireOp",EDGE,"E8");var subQ1=sQuery(id+"F0.wireOp",EDGE,"E9");Q17=makeQuery(id+"F3.boolean.opBoolean","SPLIT",EDGE,{"disambiguationData":[TD([makeQuery(id+"F3.opExtrude","SWEPT_FACE",FACE,{"disambiguationData":[OSD([sQuery(id+"F2.wireOp",EDGE,"E16.MirrorCS")])]})])],"derivedFrom":makeQuery(id+"F1.opRevolve","SWEPT_EDGE",EDGE,{"disambiguationData":[OSD([subQ0,subQ1])]})});}
            var Q18;
            {var subQ0=sQuery(id+"F0.wireOp",EDGE,"E8");var subQ1=sQuery(id+"F0.wireOp",EDGE,"E9");Q18=makeQuery(id+"F3.boolean.opBoolean","SPLIT",EDGE,{"disambiguationData":[TD([makeQuery(id+"F3.opExtrude","SWEPT_FACE",FACE,{"disambiguationData":[OSD([sQuery(id+"F2.wireOp",EDGE,"E18.MirrorCS")])]})])],"derivedFrom":makeQuery(id+"F1.opRevolve","SWEPT_EDGE",EDGE,{"disambiguationData":[OSD([subQ0,subQ1])]})});}
            var Q19;
            {var subQ0=sQuery(id+"F0.wireOp",EDGE,"E8");var subQ1=sQuery(id+"F0.wireOp",EDGE,"E9");var subQ3=makeQuery(id+"F1.opRevolve","SWEPT_EDGE",EDGE,{"disambiguationData":[OSD([subQ0,subQ1])]});Q19=makeQuery(id+"F3.boolean.opBoolean","SPLIT",EDGE,{"disambiguationData":[TD([makeQuery(id+"F3.opExtrude","SWEPT_FACE",FACE,{"disambiguationData":[OSD([sQuery(id+"F2.wireOp",EDGE,"E11")])]})])],"derivedFrom":subQ3});}
            fillet(context, id + "F4", {"entities" : qUnion([Q0, Q1, Q2, Q3, Q4, Q5, Q6, Q7, Q8, Q9, Q10, Q11, Q12, Q13, Q14, Q15, Q16, Q17, Q18, Q19]), "radius" : 2 * mm, "tangentPropagation" : true, "allowEdgeOverflow" : false});
        }
        {
            var Q0;
            Q0=qCreatedBy(makeId("Front.planeOp"),FACE);
            var sketch = newSketch(context, id + "F5", { "sketchPlane" : qUnion([Q0])});
            skLineSegment(sketch, "E281", {"start": v(0, 8) * mm, "end": v(-35, 8) * mm});
            skArc(sketch, "E282", {"start": v(-35, 8) * mm, "mid": v(-36.41, 8.59) * mm, "end": v(-37, 10) * mm});
            skLineSegment(sketch, "E283", {"start": v(-37, 10) * mm, "end": v(0, 10) * mm});
            skLineSegment(sketch, "E284", {"start": v(0, 10) * mm, "end": v(0, 8) * mm});
            skSolve(sketch);
        }
        {
            var Q0;
            Q0 = qSketchRegion(id + "F5", true);
            var Q1;
            Q1=sQuery(id+"F5.wireOp",EDGE,"E284");
            revolve(context, id + "F6", {"operationType" : NewBodyOperationType.REMOVE, "entities" : qUnion([Q0]), "axis" : qUnion([Q1]), "revolveType" : RevolveType.FULL, "oppositeDirection" : true});
        }
    });
